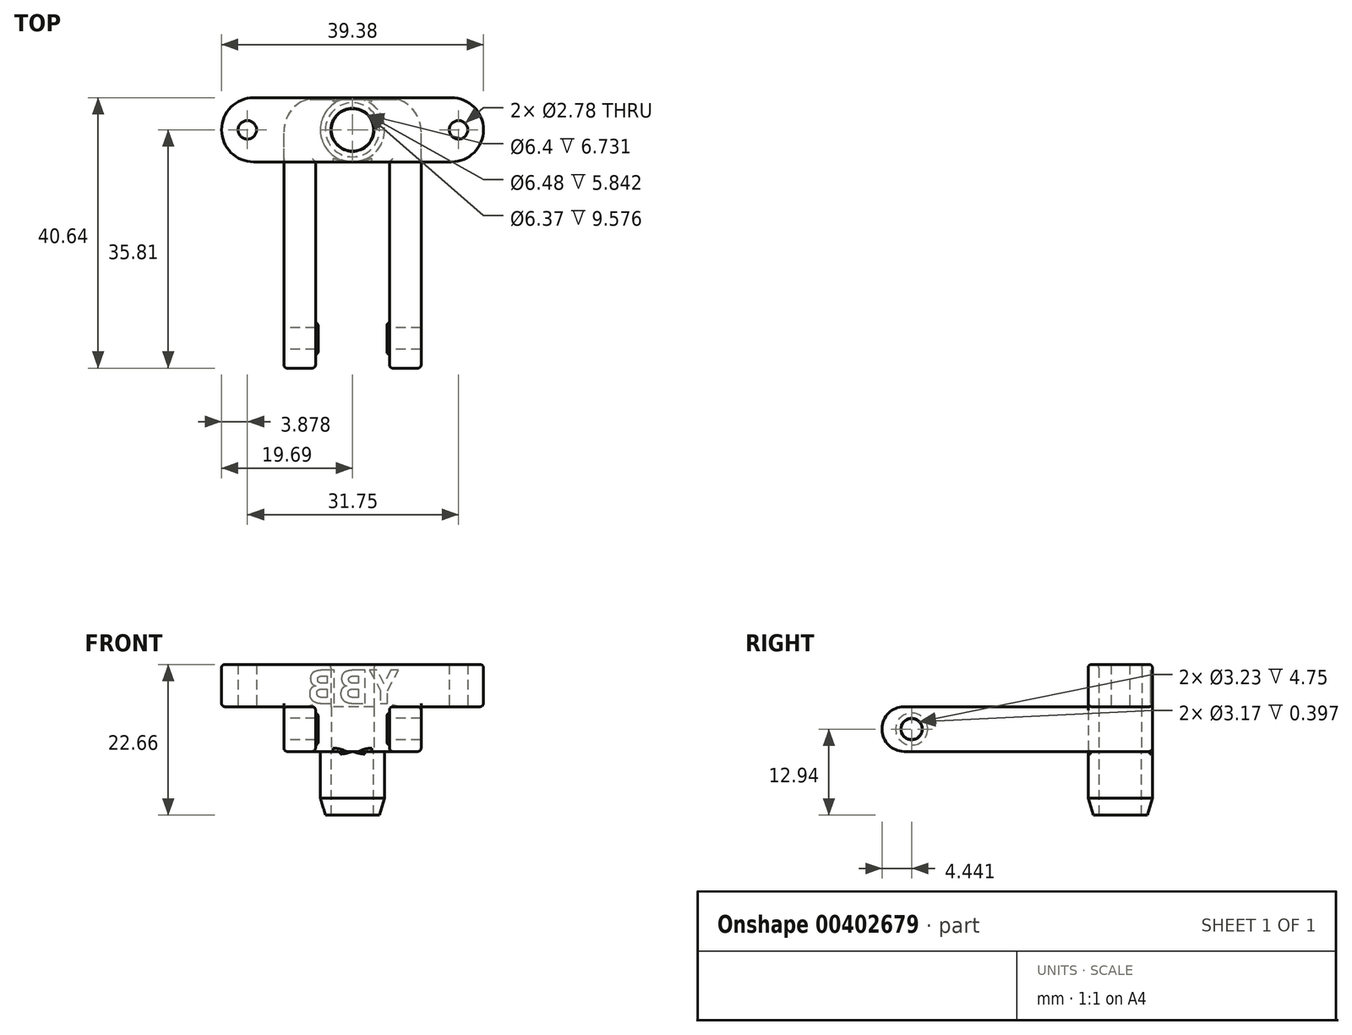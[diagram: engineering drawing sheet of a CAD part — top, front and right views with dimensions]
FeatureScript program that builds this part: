
annotation { "Feature Type Name" : "Feature", "Feature Type Description" : "" }
export const myFeature = defineFeature(function(context is Context, id is Id, definition is map)
    precondition{}
    {
        {
            var Q0;
            Q0=qCreatedBy(makeId("Top.planeOp"),FACE);
            var sketch = newSketch(context, id + "F0", { "sketchPlane" : qUnion([Q0])});
            skLineSegment(sketch, "E0.bottom", {"start": v(10.31, -4.83) * mm, "end": v(-10.31, -4.83) * mm});
            skLineSegment(sketch, "E0.top", {"start": v(10.31, 4.83) * mm, "end": v(-10.31, 4.83) * mm});
            skLineSegment(sketch, "E0.left", {"start": v(10.31, -4.83) * mm, "end": v(10.31, 4.83) * mm});
            skLineSegment(sketch, "E0.right", {"start": v(-10.31, -4.83) * mm, "end": v(-10.31, 4.83) * mm});
            skPoint(sketch, "E0.middle", {"position": v(0, 0) * mm});
            skCircle(sketch, "E1", {"center": v(0, 0) * mm, "radius": 3.2 * mm});
            skLineSegment(sketch, "E2.bottom", {"start": v(10.31, -4.83) * mm, "end": v(5.56, -4.83) * mm});
            skLineSegment(sketch, "E2.top", {"start": v(10.31, -35.81) * mm, "end": v(5.56, -35.81) * mm});
            skLineSegment(sketch, "E2.left", {"start": v(10.31, -4.83) * mm, "end": v(10.31, -35.81) * mm});
            skLineSegment(sketch, "E2.right", {"start": v(5.56, -4.83) * mm, "end": v(5.56, -35.81) * mm});
            skLineSegment(sketch, "E3.MirrorCS", {"start": v(-5.56, -4.83) * mm, "end": v(-5.56, -35.81) * mm});
            skLineSegment(sketch, "E4.MirrorCS", {"start": v(-10.31, -35.81) * mm, "end": v(-5.56, -35.81) * mm});
            skLineSegment(sketch, "E5.MirrorCS", {"start": v(-10.31, -4.83) * mm, "end": v(-10.31, -35.81) * mm});
            skSolve(sketch);
        }
        {
            var Q0;
            {var subQ8=sQuery(id+"F0.wireOp",EDGE,"E3.MirrorCS");Q0=qUnion([makeQuery(id+"F0.imprint","IMPRINT",FACE,{"disambiguationData":[TD([[makeQuery(id+"F0.imprint","IMPRINT",EDGE,{"derivedFrom":sQuery(id+"F0.wireOp",EDGE,"E0.top")}),1.0]])]}),makeQuery(id+"F0.imprint","IMPRINT",FACE,{"disambiguationData":[TD([[makeQuery(id+"F0.imprint","IMPRINT",EDGE,{"derivedFrom":subQ8}),-1.0]])]}),makeQuery(id+"F0.imprint","IMPRINT",FACE,{"disambiguationData":[TD([[makeQuery(id+"F0.imprint","IMPRINT",EDGE,{"derivedFrom":sQuery(id+"F0.wireOp",EDGE,"E2.top")}),-1.0]])]})]);}
            extrude(context, id + "F1", {"entities" : qUnion([Q0]), "endBound" : BoundingType.SYMMETRIC, "depth" : 6.73 * mm});
        }
        {
            var Q0;
            Q0=makeQuery(id+"F1.opExtrude","CAP_FACE",FACE,{"disambiguationData":[OSD([sQuery(id+"F0.wireOp",EDGE,"E0.bottom"),sQuery(id+"F0.wireOp",EDGE,"E0.top"),sQuery(id+"F0.wireOp",EDGE,"E0.left"),sQuery(id+"F0.wireOp",EDGE,"E0.right"),sQuery(id+"F0.wireOp",EDGE,"E1"),sQuery(id+"F0.wireOp",EDGE,"E2.top"),sQuery(id+"F0.wireOp",EDGE,"E2.left"),sQuery(id+"F0.wireOp",EDGE,"E2.right"),sQuery(id+"F0.wireOp",EDGE,"E3.MirrorCS"),sQuery(id+"F0.wireOp",EDGE,"E4.MirrorCS"),sQuery(id+"F0.wireOp",EDGE,"E5.MirrorCS")])],"isStart":true});
            var sketch = newSketch(context, id + "F2", { "sketchPlane" : qUnion([Q0])});
            skCircle(sketch, "E6", {"center": v(0, 0) * mm, "radius": 4.83 * mm});
            skCircle(sketch, "E7", {"center": v(0, 0) * mm, "radius": 3.15 * mm});
            skSolve(sketch);
        }
        {
            var Q0;
            Q0=makeQuery(id+"F1.opExtrude","SWEPT_FACE",FACE,{"disambiguationData":[OSD([sQuery(id+"F0.wireOp",EDGE,"E0.right"),sQuery(id+"F0.wireOp",EDGE,"E5.MirrorCS")])]});
            var sketch = newSketch(context, id + "F3", { "sketchPlane" : qUnion([Q0])});
            skCircle(sketch, "E8", {"center": v(31.37, 0) * mm, "radius": 1.61 * mm});
            skSolve(sketch);
        }
        {
            var Q0;
            Q0=qSketchRegion(id+"F3",true);
            extrude(context, id + "F4", {"entities" : qUnion([Q0]), "operationType" : NewBodyOperationType.REMOVE, "endBound" : BoundingType.THROUGH_ALL, "oppositeDirection" : true, "depth" : 25.4 * mm});
        }
        {
            var Q0;
            Q0=qSketchRegion(id+"F2",true);
            extrude(context, id + "F5", {"entities" : qUnion([Q0]), "operationType" : NewBodyOperationType.ADD, "depth" : 9.58 * mm});
        }
        {
            var Q0;
            Q0=makeQuery(id+"F1.opExtrude","SWEPT_FACE",FACE,{"disambiguationData":[OSD([sQuery(id+"F0.wireOp",EDGE,"E3.MirrorCS")])]});
            var sketch = newSketch(context, id + "F6", { "sketchPlane" : qUnion([Q0])});
            skCircle(sketch, "E9", {"center": v(-31.37, 0) * mm, "radius": 1.59 * mm});
            skCircle(sketch, "E10", {"center": v(-31.37, 0) * mm, "radius": 2.41 * mm});
            skSolve(sketch);
        }
        {
            var Q0;
            Q0=qSketchRegion(id+"F6",true);
            extrude(context, id + "F7", {"entities" : qUnion([Q0]), "operationType" : NewBodyOperationType.ADD, "depth" : 0.4 * mm, "offsetDistance" : 25.4 * mm});
        }
        {
            var Q0;
            Q0=makeQuery(id+"F1.opExtrude","SWEPT_FACE",FACE,{"disambiguationData":[OSD([sQuery(id+"F0.wireOp",EDGE,"E2.right")])]});
            var sketch = newSketch(context, id + "F8", { "sketchPlane" : qUnion([Q0])});
            skCircle(sketch, "E11", {"center": v(31.37, 0) * mm, "radius": 1.59 * mm});
            skCircle(sketch, "E12", {"center": v(31.37, 0) * mm, "radius": 2.41 * mm});
            skSolve(sketch);
        }
        {
            var Q0;
            Q0=qSketchRegion(id+"F8",true);
            extrude(context, id + "F9", {"entities" : qUnion([Q0]), "operationType" : NewBodyOperationType.ADD, "depth" : 0.4 * mm, "offsetDistance" : 25.4 * mm});
        }
        {
            var Q0;
            Q0=makeQuery(id+"F1.opExtrude","CAP_FACE",FACE,{"disambiguationData":[OSD([sQuery(id+"F0.wireOp",EDGE,"E0.bottom"),sQuery(id+"F0.wireOp",EDGE,"E0.top"),sQuery(id+"F0.wireOp",EDGE,"E0.left"),sQuery(id+"F0.wireOp",EDGE,"E0.right"),sQuery(id+"F0.wireOp",EDGE,"E1"),sQuery(id+"F0.wireOp",EDGE,"E2.top"),sQuery(id+"F0.wireOp",EDGE,"E2.left"),sQuery(id+"F0.wireOp",EDGE,"E2.right"),sQuery(id+"F0.wireOp",EDGE,"E3.MirrorCS"),sQuery(id+"F0.wireOp",EDGE,"E4.MirrorCS"),sQuery(id+"F0.wireOp",EDGE,"E5.MirrorCS")])],"isStart":false});
            var sketch = newSketch(context, id + "F10", { "sketchPlane" : qUnion([Q0])});
            skLineSegment(sketch, "E13.bottom", {"start": v(19.69, -4.83) * mm, "end": v(-19.69, -4.83) * mm});
            skLineSegment(sketch, "E13.top", {"start": v(19.68, 4.83) * mm, "end": v(-19.69, 4.83) * mm});
            skLineSegment(sketch, "E13.left", {"start": v(19.69, -4.83) * mm, "end": v(19.69, 4.83) * mm});
            skLineSegment(sketch, "E13.right", {"start": v(-19.69, -4.83) * mm, "end": v(-19.69, 4.83) * mm});
            skPoint(sketch, "E13.middle", {"position": v(0, 0) * mm});
            skCircle(sketch, "E14", {"center": v(0, 0) * mm, "radius": 3.24 * mm});
            skCircle(sketch, "E15", {"center": v(15.94, 0) * mm, "radius": 1.39 * mm});
            skCircle(sketch, "E16", {"center": v(-15.81, 0) * mm, "radius": 1.39 * mm});
            skSolve(sketch);
        }
        {
            var Q0;
            Q0=qSketchRegion(id+"F10",true);
            extrude(context, id + "F11", {"entities" : qUnion([Q0]), "operationType" : NewBodyOperationType.ADD, "depth" : 6.35 * mm});
        }
        {
            var Q0;
            Q0=makeQuery(id+"F11.opExtrude","CAP_EDGE",EDGE,{"disambiguationData":[OSD([sQuery(id+"F10.wireOp",EDGE,"E13.left")])],"isStart":false});
            var Q1;
            Q1=makeQuery(id+"F11.opExtrude","CAP_EDGE",EDGE,{"disambiguationData":[OSD([sQuery(id+"F10.wireOp",EDGE,"E13.top")])],"isStart":false});
            var Q2;
            Q2=makeQuery(id+"F11.opExtrude","CAP_EDGE",EDGE,{"disambiguationData":[OSD([sQuery(id+"F10.wireOp",EDGE,"E13.right")])],"isStart":false});
            var Q3;
            Q3=makeQuery(id+"F11.opExtrude","CAP_EDGE",EDGE,{"disambiguationData":[OSD([sQuery(id+"F10.wireOp",EDGE,"E13.bottom")])],"isStart":false});
            var Q4;
            Q4=makeQuery(id+"F11.opExtrude","CAP_EDGE",EDGE,{"disambiguationData":[OSD([sQuery(id+"F10.wireOp",EDGE,"E14")])],"isStart":false});
            var Q5;
            {var subQ0=sQuery(id+"F10.wireOp",EDGE,"E13.bottom");var subQ1=makeQuery(id+"F11.opExtrude","SWEPT_FACE",FACE,{"disambiguationData":[OSD([subQ0])]});var subQ4=sQuery(id+"F0.wireOp",EDGE,"E0.bottom");var subQ5=makeQuery(id+"F1.opExtrude","SWEPT_FACE",FACE,{"disambiguationData":[OSD([subQ4])]});var subQ6=sQuery(id+"F10.wireOp",EDGE,"E13.right");var subQ7=makeQuery(id+"F11.opExtrude","CAP_FACE",FACE,{"disambiguationData":[OSD([subQ0,sQuery(id+"F10.wireOp",EDGE,"E13.top"),sQuery(id+"F10.wireOp",EDGE,"E13.left"),subQ6,sQuery(id+"F10.wireOp",EDGE,"E14"),sQuery(id+"F10.wireOp",EDGE,"E15"),sQuery(id+"F10.wireOp",EDGE,"E16")])],"isStart":true});Q5=makeQuery(id+"F11.boolean.opBoolean","SPLIT",EDGE,{"disambiguationData":[topologyDisambiguationEdgeConnected([subQ5,subQ1,subQ7]),TD([makeQuery(id+"F11.opExtrude","SWEPT_FACE",FACE,{"disambiguationData":[OSD([subQ6])]})])],"derivedFrom":makeQuery(id+"F11.opExtrude","CAP_EDGE",EDGE,{"disambiguationData":[OSD([subQ0])],"isStart":true})});}
            var Q6;
            {var subQ0=sQuery(id+"F10.wireOp",EDGE,"E13.bottom");var subQ1=makeQuery(id+"F11.opExtrude","SWEPT_FACE",FACE,{"disambiguationData":[OSD([subQ0])]});var subQ4=sQuery(id+"F0.wireOp",EDGE,"E0.bottom");var subQ5=makeQuery(id+"F1.opExtrude","SWEPT_FACE",FACE,{"disambiguationData":[OSD([subQ4])]});var subQ6=sQuery(id+"F10.wireOp",EDGE,"E13.left");var subQ7=makeQuery(id+"F11.opExtrude","CAP_FACE",FACE,{"disambiguationData":[OSD([subQ0,sQuery(id+"F10.wireOp",EDGE,"E13.top"),subQ6,sQuery(id+"F10.wireOp",EDGE,"E13.right"),sQuery(id+"F10.wireOp",EDGE,"E14"),sQuery(id+"F10.wireOp",EDGE,"E15"),sQuery(id+"F10.wireOp",EDGE,"E16")])],"isStart":true});Q6=makeQuery(id+"F11.boolean.opBoolean","SPLIT",EDGE,{"disambiguationData":[topologyDisambiguationEdgeConnected([subQ5,subQ1,subQ7]),TD([makeQuery(id+"F11.opExtrude","SWEPT_FACE",FACE,{"disambiguationData":[OSD([subQ6])]})])],"derivedFrom":makeQuery(id+"F11.opExtrude","CAP_EDGE",EDGE,{"disambiguationData":[OSD([subQ0])],"isStart":true})});}
            var Q7;
            Q7=makeQuery(id+"F11.opExtrude","CAP_EDGE",EDGE,{"disambiguationData":[OSD([sQuery(id+"F10.wireOp",EDGE,"E13.left")])],"isStart":true});
            var Q8;
            {var subQ0=sQuery(id+"F10.wireOp",EDGE,"E13.top");var subQ1=sQuery(id+"F10.wireOp",EDGE,"E13.left");Q8=makeQuery(id+"F11.boolean.opBoolean","SPLIT",EDGE,{"disambiguationData":[TD([makeQuery(id+"F11.opExtrude","SWEPT_FACE",FACE,{"disambiguationData":[OSD([subQ1])]})])],"derivedFrom":makeQuery(id+"F11.opExtrude","CAP_EDGE",EDGE,{"disambiguationData":[OSD([subQ0])],"isStart":true})});}
            var Q9;
            {var subQ0=sQuery(id+"F10.wireOp",EDGE,"E13.top");var subQ1=sQuery(id+"F10.wireOp",EDGE,"E13.right");Q9=makeQuery(id+"F11.boolean.opBoolean","SPLIT",EDGE,{"disambiguationData":[TD([makeQuery(id+"F11.opExtrude","SWEPT_FACE",FACE,{"disambiguationData":[OSD([subQ1])]})])],"derivedFrom":makeQuery(id+"F11.opExtrude","CAP_EDGE",EDGE,{"disambiguationData":[OSD([subQ0])],"isStart":true})});}
            var Q10;
            Q10=makeQuery(id+"F11.opExtrude","CAP_EDGE",EDGE,{"disambiguationData":[OSD([sQuery(id+"F10.wireOp",EDGE,"E13.right")])],"isStart":true});
            fillet(context, id + "F12", {"entities" : qUnion([Q0, Q1, Q2, Q3, Q4, Q5, Q6, Q7, Q8, Q9, Q10]), "radius" : 0.5 * mm, "allowEdgeOverflow" : false});
        }
        {
            var Q0;
            Q0=makeQuery(id+"F1.opExtrude","CAP_EDGE",EDGE,{"disambiguationData":[OSD([sQuery(id+"F0.wireOp",EDGE,"E3.MirrorCS")])],"isStart":false});
            var Q1;
            Q1=makeQuery(id+"F7.opExtrude","CAP_EDGE",EDGE,{"disambiguationData":[OSD([sQuery(id+"F6.wireOp",EDGE,"E10")])],"isStart":false});
            var Q2;
            Q2=makeQuery(id+"F1.opExtrude","CAP_EDGE",EDGE,{"disambiguationData":[OSD([sQuery(id+"F0.wireOp",EDGE,"E2.right")])],"isStart":false});
            var Q3;
            Q3=makeQuery(id+"F9.opExtrude","CAP_EDGE",EDGE,{"disambiguationData":[OSD([sQuery(id+"F8.wireOp",EDGE,"E12")])],"isStart":false});
            fillet(context, id + "F13", {"entities" : qUnion([Q0, Q1, Q2, Q3]), "radius" : 0.5 * mm, "tangentPropagation" : true, "allowEdgeOverflow" : false});
        }
        {
            var Q0;
            Q0=makeQuery(id+"F5.boolean.opBoolean","SPLIT",EDGE,{"disambiguationData":[OD(0.0)],"derivedFrom":makeQuery(id+"F5.opExtrude","CAP_EDGE",EDGE,{"disambiguationData":[OSD([sQuery(id+"F2.wireOp",EDGE,"E6")])],"isStart":true})});
            var Q1;
            Q1=makeQuery(id+"F5.boolean.opBoolean","SPLIT",EDGE,{"disambiguationData":[OD(1.0)],"derivedFrom":makeQuery(id+"F5.opExtrude","CAP_EDGE",EDGE,{"disambiguationData":[OSD([sQuery(id+"F2.wireOp",EDGE,"E6")])],"isStart":true})});
            fillet(context, id + "F14", {"entities" : qUnion([Q0, Q1]), "radius" : 0.38 * mm, "tangentPropagation" : true, "allowEdgeOverflow" : false});
        }
        {
            var Q0;
            Q0=makeQuery(id+"F1.opExtrude","SWEPT_EDGE",EDGE,{"disambiguationData":[OSD([sQuery(id+"F0.wireOp",EDGE,"E3.MirrorCS"),sQuery(id+"F0.wireOp",EDGE,"E4.MirrorCS")])]});
            var Q1;
            Q1=makeQuery(id+"F1.opExtrude","SWEPT_EDGE",EDGE,{"disambiguationData":[OSD([sQuery(id+"F0.wireOp",EDGE,"E2.top"),sQuery(id+"F0.wireOp",EDGE,"E2.right")])]});
            var Q2;
            {var subQ0=sQuery(id+"F0.wireOp",EDGE,"E5.MirrorCS");var subQ1=sQuery(id+"F0.wireOp",EDGE,"E0.right");Q2=makeQuery(id+"F11.boolean.opBoolean","SPLIT",EDGE,{"disambiguationData":[topologyDisambiguationEdgeConnected([makeQuery(id+"F1.opExtrude","CAP_FACE",FACE,{"disambiguationData":[OSD([sQuery(id+"F0.wireOp",EDGE,"E0.bottom"),sQuery(id+"F0.wireOp",EDGE,"E0.top"),sQuery(id+"F0.wireOp",EDGE,"E0.left"),subQ1,sQuery(id+"F0.wireOp",EDGE,"E1"),sQuery(id+"F0.wireOp",EDGE,"E2.top"),sQuery(id+"F0.wireOp",EDGE,"E2.left"),sQuery(id+"F0.wireOp",EDGE,"E2.right"),sQuery(id+"F0.wireOp",EDGE,"E3.MirrorCS"),sQuery(id+"F0.wireOp",EDGE,"E4.MirrorCS"),subQ0])],"isStart":false})])],"derivedFrom":makeQuery(id+"F1.opExtrude","CAP_EDGE",EDGE,{"disambiguationData":[OSD([subQ1,subQ0])],"isStart":false})});}
            var Q3;
            Q3=makeQuery(id+"F1.opExtrude","SWEPT_EDGE",EDGE,{"disambiguationData":[OSD([sQuery(id+"F0.wireOp",EDGE,"E4.MirrorCS"),sQuery(id+"F0.wireOp",EDGE,"E5.MirrorCS")])]});
            var Q4;
            Q4=makeQuery(id+"F1.opExtrude","CAP_EDGE",EDGE,{"disambiguationData":[OSD([sQuery(id+"F0.wireOp",EDGE,"E0.right"),sQuery(id+"F0.wireOp",EDGE,"E5.MirrorCS")])],"isStart":true});
            var Q5;
            {var subQ0=sQuery(id+"F0.wireOp",EDGE,"E5.MirrorCS");var subQ1=sQuery(id+"F0.wireOp",EDGE,"E0.right");var subQ2=sQuery(id+"F0.wireOp",EDGE,"E0.top");Q5=makeQuery(id+"F5.boolean.opBoolean","SPLIT",EDGE,{"disambiguationData":[TD([makeQuery(id+"F1.opExtrude","SWEPT_FACE",FACE,{"disambiguationData":[OSD([subQ1,subQ0])]})])],"derivedFrom":makeQuery(id+"F1.opExtrude","CAP_EDGE",EDGE,{"disambiguationData":[OSD([subQ2])],"isStart":true})});}
            var Q6;
            {var subQ0=sQuery(id+"F0.wireOp",EDGE,"E2.left");var subQ1=sQuery(id+"F0.wireOp",EDGE,"E0.left");var subQ2=sQuery(id+"F0.wireOp",EDGE,"E0.top");Q6=makeQuery(id+"F5.boolean.opBoolean","SPLIT",EDGE,{"disambiguationData":[TD([makeQuery(id+"F1.opExtrude","SWEPT_FACE",FACE,{"disambiguationData":[OSD([subQ1,subQ0])]})])],"derivedFrom":makeQuery(id+"F1.opExtrude","CAP_EDGE",EDGE,{"disambiguationData":[OSD([subQ2])],"isStart":true})});}
            var Q7;
            {var subQ0=sQuery(id+"F0.wireOp",EDGE,"E0.bottom");var subQ1=sQuery(id+"F0.wireOp",EDGE,"E3.MirrorCS");Q7=makeQuery(id+"F5.boolean.opBoolean","SPLIT",EDGE,{"disambiguationData":[TD([makeQuery(id+"F1.opExtrude","SWEPT_FACE",FACE,{"disambiguationData":[OSD([subQ1])]})])],"derivedFrom":makeQuery(id+"F1.opExtrude","CAP_EDGE",EDGE,{"disambiguationData":[OSD([subQ0])],"isStart":true})});}
            var Q8;
            Q8=makeQuery(id+"F1.opExtrude","CAP_EDGE",EDGE,{"disambiguationData":[OSD([sQuery(id+"F0.wireOp",EDGE,"E3.MirrorCS")])],"isStart":true});
            var Q9;
            {var subQ0=sQuery(id+"F0.wireOp",EDGE,"E0.bottom");var subQ1=sQuery(id+"F0.wireOp",EDGE,"E2.right");Q9=makeQuery(id+"F5.boolean.opBoolean","SPLIT",EDGE,{"disambiguationData":[TD([makeQuery(id+"F1.opExtrude","SWEPT_FACE",FACE,{"disambiguationData":[OSD([subQ1])]})])],"derivedFrom":makeQuery(id+"F1.opExtrude","CAP_EDGE",EDGE,{"disambiguationData":[OSD([subQ0])],"isStart":true})});}
            var Q10;
            Q10=makeQuery(id+"F1.opExtrude","CAP_EDGE",EDGE,{"disambiguationData":[OSD([sQuery(id+"F0.wireOp",EDGE,"E2.right")])],"isStart":true});
            var Q11;
            Q11=makeQuery(id+"F1.opExtrude","CAP_EDGE",EDGE,{"disambiguationData":[OSD([sQuery(id+"F0.wireOp",EDGE,"E0.left"),sQuery(id+"F0.wireOp",EDGE,"E2.left")])],"isStart":true});
            var Q12;
            Q12=makeQuery(id+"F1.opExtrude","SWEPT_EDGE",EDGE,{"disambiguationData":[OSD([sQuery(id+"F0.wireOp",EDGE,"E2.top"),sQuery(id+"F0.wireOp",EDGE,"E2.left")])]});
            var Q13;
            {var subQ0=sQuery(id+"F0.wireOp",EDGE,"E2.left");var subQ1=sQuery(id+"F0.wireOp",EDGE,"E0.left");Q13=makeQuery(id+"F11.boolean.opBoolean","SPLIT",EDGE,{"disambiguationData":[topologyDisambiguationEdgeConnected([makeQuery(id+"F1.opExtrude","CAP_FACE",FACE,{"disambiguationData":[OSD([sQuery(id+"F0.wireOp",EDGE,"E0.bottom"),sQuery(id+"F0.wireOp",EDGE,"E0.top"),subQ1,sQuery(id+"F0.wireOp",EDGE,"E0.right"),sQuery(id+"F0.wireOp",EDGE,"E1"),sQuery(id+"F0.wireOp",EDGE,"E2.top"),subQ0,sQuery(id+"F0.wireOp",EDGE,"E2.right"),sQuery(id+"F0.wireOp",EDGE,"E3.MirrorCS"),sQuery(id+"F0.wireOp",EDGE,"E4.MirrorCS"),sQuery(id+"F0.wireOp",EDGE,"E5.MirrorCS")])],"isStart":false})])],"derivedFrom":makeQuery(id+"F1.opExtrude","CAP_EDGE",EDGE,{"disambiguationData":[OSD([subQ1,subQ0])],"isStart":false})});}
            fillet(context, id + "F15", {"entities" : qUnion([Q0, Q1, Q2, Q3, Q4, Q5, Q6, Q7, Q8, Q9, Q10, Q11, Q12, Q13]), "radius" : 0.5 * mm, "allowEdgeOverflow" : false});
        }
        {
            var Q0;
            Q0=makeQuery(id+"F1.opExtrude","CAP_EDGE",EDGE,{"disambiguationData":[OSD([sQuery(id+"F0.wireOp",EDGE,"E4.MirrorCS")])],"isStart":true});
            var Q1;
            Q1=makeQuery(id+"F1.opExtrude","CAP_EDGE",EDGE,{"disambiguationData":[OSD([sQuery(id+"F0.wireOp",EDGE,"E2.top")])],"isStart":true});
            var Q2;
            Q2=makeQuery(id+"F1.opExtrude","CAP_EDGE",EDGE,{"disambiguationData":[OSD([sQuery(id+"F0.wireOp",EDGE,"E2.top")])],"isStart":false});
            var Q3;
            Q3=makeQuery(id+"F1.opExtrude","CAP_EDGE",EDGE,{"disambiguationData":[OSD([sQuery(id+"F0.wireOp",EDGE,"E4.MirrorCS")])],"isStart":false});
            fillet(context, id + "F16", {"entities" : qUnion([Q0, Q1, Q2, Q3]), "radius" : 3.3 * mm, "tangentPropagation" : true, "allowEdgeOverflow" : false});
        }
        {
            var Q0;
            Q0=makeQuery(id+"F11.opExtrude","SWEPT_EDGE",EDGE,{"disambiguationData":[OSD([sQuery(id+"F10.wireOp",EDGE,"E13.bottom"),sQuery(id+"F10.wireOp",EDGE,"E13.right")])]});
            var Q1;
            Q1=makeQuery(id+"F11.opExtrude","SWEPT_EDGE",EDGE,{"disambiguationData":[OSD([sQuery(id+"F10.wireOp",EDGE,"E13.top"),sQuery(id+"F10.wireOp",EDGE,"E13.right")])]});
            var Q2;
            Q2=makeQuery(id+"F11.opExtrude","SWEPT_EDGE",EDGE,{"disambiguationData":[OSD([sQuery(id+"F10.wireOp",EDGE,"E13.top"),sQuery(id+"F10.wireOp",EDGE,"E13.left")])]});
            var Q3;
            Q3=makeQuery(id+"F11.opExtrude","SWEPT_EDGE",EDGE,{"disambiguationData":[OSD([sQuery(id+"F10.wireOp",EDGE,"E13.bottom"),sQuery(id+"F10.wireOp",EDGE,"E13.left")])]});
            fillet(context, id + "F17", {"entities" : qUnion([Q0, Q1, Q2, Q3]), "radius" : 4.83 * mm, "tangentPropagation" : true, "allowEdgeOverflow" : false});
        }
        {
            var Q0;
            Q0=makeQuery(id+"F1.opExtrude","SWEPT_EDGE",EDGE,{"disambiguationData":[OSD([sQuery(id+"F0.wireOp",EDGE,"E0.top"),sQuery(id+"F0.wireOp",EDGE,"E0.left")])]});
            var Q1;
            Q1=makeQuery(id+"F1.opExtrude","SWEPT_EDGE",EDGE,{"disambiguationData":[OSD([sQuery(id+"F0.wireOp",EDGE,"E0.top"),sQuery(id+"F0.wireOp",EDGE,"E0.right")])]});
            fillet(context, id + "F18", {"entities" : qUnion([Q0, Q1]), "radius" : 5.08 * mm, "tangentPropagation" : true, "allowEdgeOverflow" : false});
        }
        {
            var Q0;
            Q0=makeQuery(id+"F5.opExtrude","CAP_EDGE",EDGE,{"disambiguationData":[OSD([sQuery(id+"F2.wireOp",EDGE,"E6")])],"isStart":false});
            chamfer(context, id + "F19", {"entities" : qUnion([Q0]), "chamferType" : ChamferType.TWO_OFFSETS, "width1" : 0.76 * mm, "oppositeDirection" : false, "width2" : 2.54 * mm, "tangentPropagation" : true});
        }
        {
            var Q0;
            Q0=makeQuery(id+"F11.opExtrude","CAP_FACE",FACE,{"disambiguationData":[OSD([sQuery(id+"F10.wireOp",EDGE,"E13.bottom"),sQuery(id+"F10.wireOp",EDGE,"E13.top"),sQuery(id+"F10.wireOp",EDGE,"E13.left"),sQuery(id+"F10.wireOp",EDGE,"E13.right"),sQuery(id+"F10.wireOp",EDGE,"E14"),sQuery(id+"F10.wireOp",EDGE,"E15"),sQuery(id+"F10.wireOp",EDGE,"5532dd9e-91bd-412b-a6f8-db201805de330.MirrorC")])],"isStart":false});
            var sketch = newSketch(context, id + "F20", { "sketchPlane" : qUnion([Q0])});
            skCircle(sketch, "E17", {"center": v(0, 0) * mm, "radius": 3.18 * mm});
            skSolve(sketch);
        }
        {
            var Q0;
            Q0=qSketchRegion(id+"F20",true);
            extrude(context, id + "F21", {"entities" : qUnion([Q0]), "operationType" : NewBodyOperationType.REMOVE, "oppositeDirection" : true, "depth" : 38.1 * mm});
        }
        {
            var Q0;
            Q0=makeQuery(id+"F11.boolean.opBoolean","MERGE",FACE,{"derivedFrom":[makeQuery(id+"F1.opExtrude","SWEPT_FACE",FACE,{"disambiguationData":[OSD([sQuery(id+"F0.wireOp",EDGE,"E0.top")])]}),makeQuery(id+"F11.opExtrude","SWEPT_FACE",FACE,{"disambiguationData":[OSD([sQuery(id+"F10.wireOp",EDGE,"E13.top")])]})]});
            var sketch = newSketch(context, id + "F22", { "sketchPlane" : qUnion([Q0])});
            skText(sketch, "E18", { "text": "YBB", "fontName": "OpenSans-Bold.ttf"});
            const initialGuessF22  = {"E18": [-0.0069, 0.00387, 1, 0, 0.00502]};
            skSetInitialGuess(sketch, initialGuessF22);
            skSolve(sketch);
        }
        {
            var Q0;
            Q0=qSketchRegion(id+"F22",true);
            extrude(context, id + "F23", {"entities" : qUnion([Q0]), "operationType" : NewBodyOperationType.REMOVE, "oppositeDirection" : true, "depth" : 0.25 * mm, "offsetDistance" : 25.4 * mm});
        }
    });
